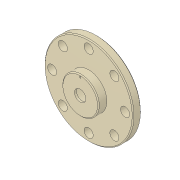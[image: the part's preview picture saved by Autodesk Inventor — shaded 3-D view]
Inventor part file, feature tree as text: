
AUTODESK INVENTOR PART (.ipt)
format: ipt  version: 2019.4 (Build 234330000, 330)  size: 173,056 bytes
history: native  units: mm
features: sketch x3, hole x2, other x1, revolve x1, chamfer x1
ambient origin geometry x8: Origin, YZ Plane, XZ Plane, XY Plane, X Axis, Y Axis, Z Axis, Center Point
bodies: Body1 (feature_tree)
feature tree (8):
  other  "ソリッド1"
  revolve  "回転1"
  hole  "穴1"  [1 undecoded]
  chamfer  "面取り1"  Distance=18.0mm
  hole  "穴2"  [1 undecoded]
  sketch  "スケッチ1"
  sketch  "スケッチ2"
  sketch  "スケッチ3"
note: 2 required parameter values undecoded (feature->parameter linkage not recoverable at this tier; creation-order binding heuristic only, values carry confidence <= 0.55)
